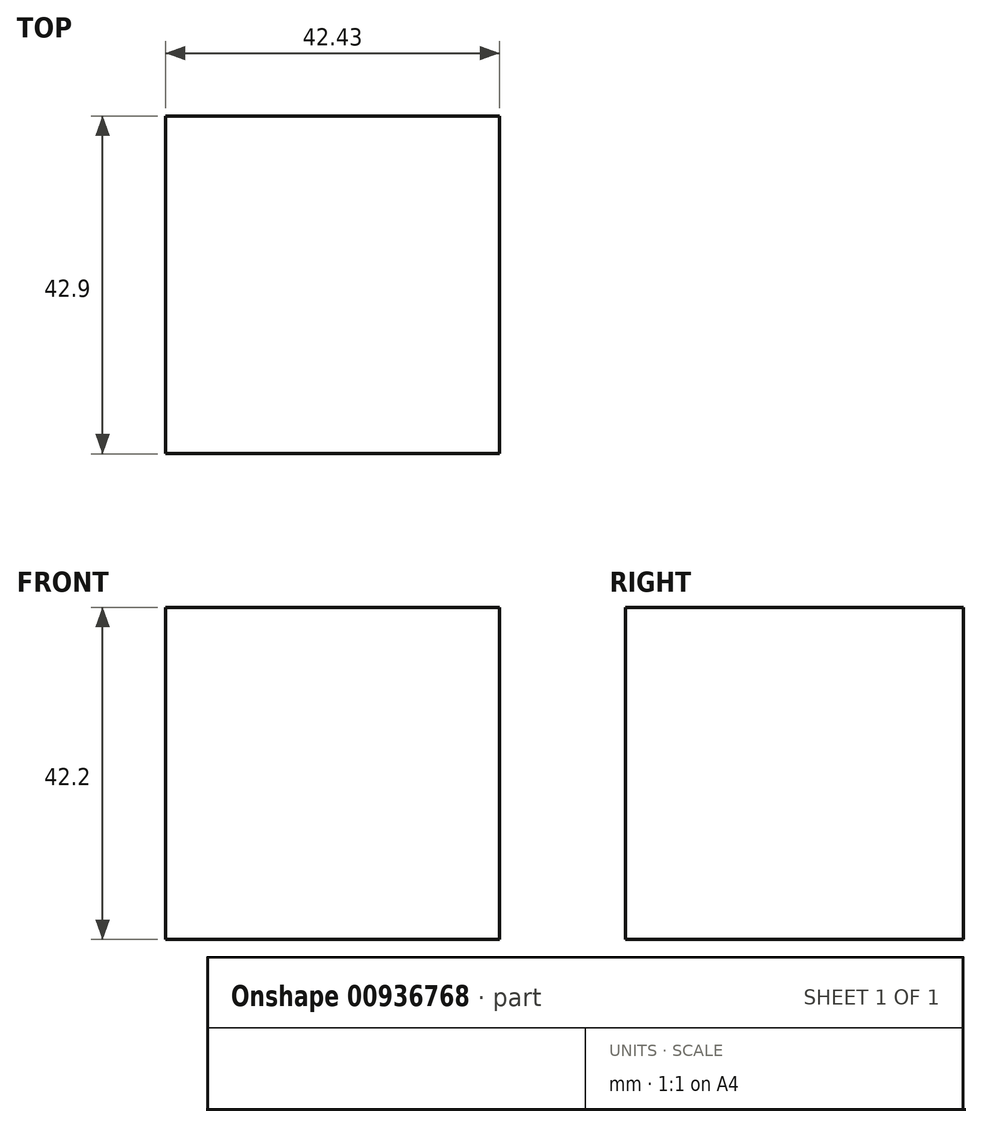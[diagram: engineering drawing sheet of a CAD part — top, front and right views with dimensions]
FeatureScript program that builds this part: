
annotation { "Feature Type Name" : "Feature", "Feature Type Description" : "" }
export const myFeature = defineFeature(function(context is Context, id is Id, definition is map)
    precondition{}
    {
        {
            var Q0;
            Q0=qCreatedBy(makeId("Top.planeOp"),FACE);
            var sketch = newSketch(context, id + "F0", { "sketchPlane" : qUnion([Q0])});
            skLineSegment(sketch, "E0", {"start": v(-55.3, 46.55) * mm, "end": v(-12.88, 46.55) * mm});
            skLineSegment(sketch, "E1", {"start": v(-12.88, 46.55) * mm, "end": v(-12.88, 3.65) * mm});
            skLineSegment(sketch, "E2", {"start": v(-12.88, 3.65) * mm, "end": v(-52.6, 3.65) * mm});
            skLineSegment(sketch, "E3", {"start": v(-55.3, 46.55) * mm, "end": v(-55.3, 3.65) * mm});
            skLineSegment(sketch, "E4", {"start": v(-52.6, 3.65) * mm, "end": v(-55.3, 3.65) * mm});
            skLineSegment(sketch, "E5", {"start": v(-122.6, 28.2) * mm, "end": v(-120.45, 25.04) * mm});
            skSolve(sketch);
        }
        {
            var Q0;
            Q0 = qSketchRegion(id + "F0", true);
            extrude(context, id + "F1", {"entities" : qUnion([Q0]), "oppositeDirection" : true, "depth" : 42.2 * mm, "offsetDistance" : 25 * mm});
        }
    });
